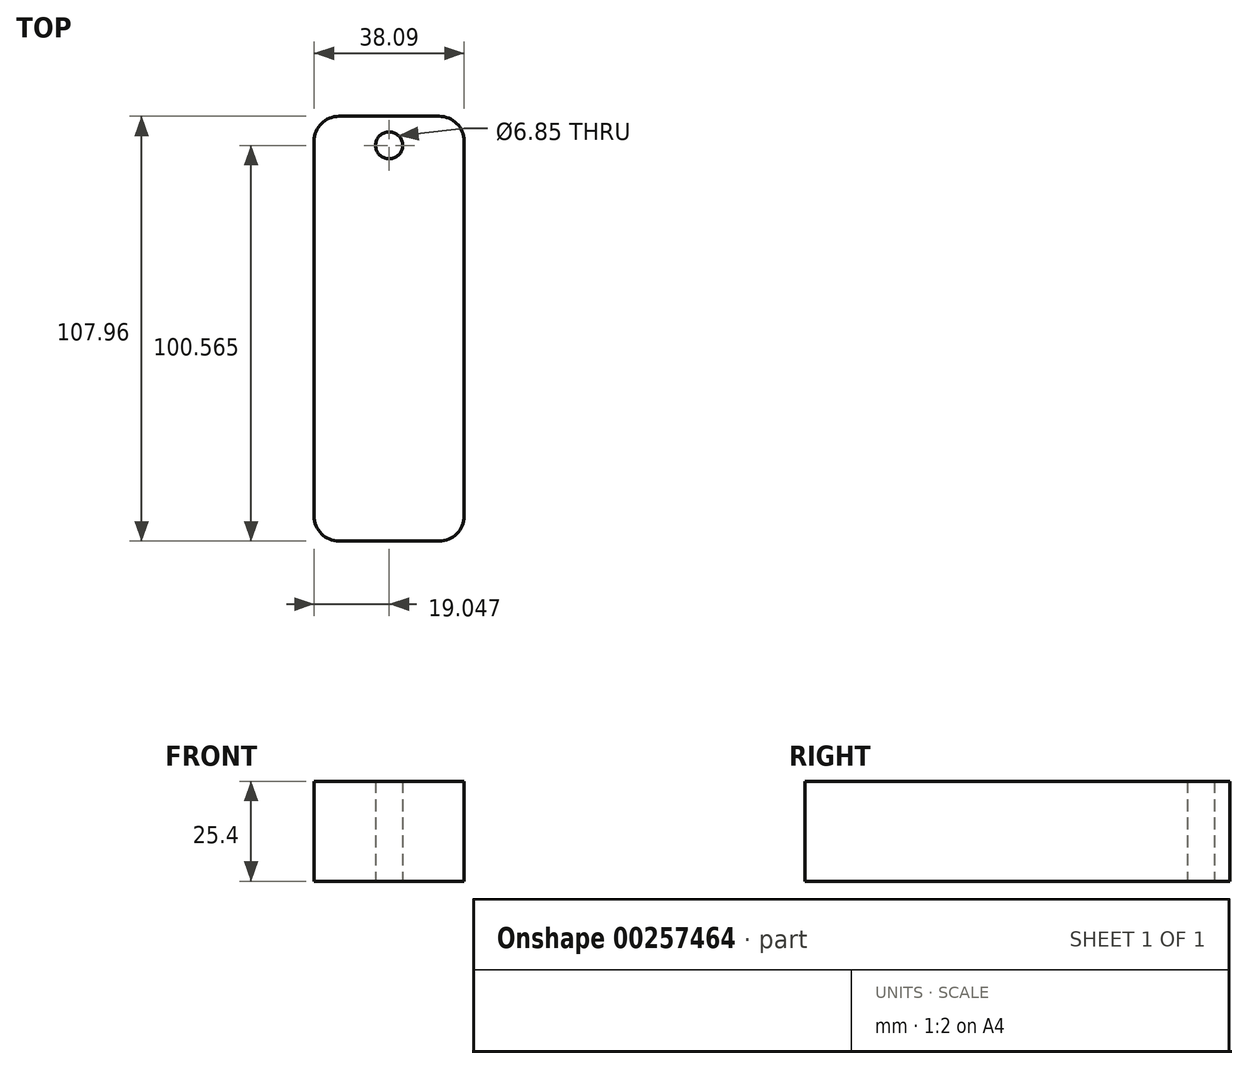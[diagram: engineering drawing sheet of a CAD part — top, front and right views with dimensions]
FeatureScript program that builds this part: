
annotation { "Feature Type Name" : "Feature", "Feature Type Description" : "" }
export const myFeature = defineFeature(function(context is Context, id is Id, definition is map)
    precondition{}
    {
        {
            var Q0;
            Q0=qCreatedBy(makeId("Top.planeOp"),FACE);
            var sketch = newSketch(context, id + "F0", { "sketchPlane" : qUnion([Q0])});
            skLineSegment(sketch, "E0.bottom", {"start": v(-19.4, 35.07) * mm, "end": v(5.98, 35.07) * mm});
            skLineSegment(sketch, "E0.top", {"start": v(-19.4, -72.89) * mm, "end": v(5.98, -72.89) * mm});
            skLineSegment(sketch, "E0.left", {"start": v(-25.76, 28.72) * mm, "end": v(-25.76, -66.54) * mm});
            skLineSegment(sketch, "E0.right", {"start": v(12.33, 28.72) * mm, "end": v(12.33, -66.54) * mm});
            skCircle(sketch, "E1", {"center": v(-6.71, 27.67) * mm, "radius": 3.43 * mm});
            skPoint(sketch, "E1.centerSnap0", {"position": v(-6.71, 35.07) * mm});
            skPoint(sketch, "E2.visualSharp", {"position": v(-25.76, 35.07) * mm});
            skArc(sketch, "E2.filletArc", {"start": v(-19.4, 35.07) * mm, "mid": v(-23.9, 33.21) * mm, "end": v(-25.76, 28.72) * mm});
            skPoint(sketch, "E3.visualSharp", {"position": v(12.33, 35.07) * mm});
            skArc(sketch, "E3.filletArc", {"start": v(12.33, 28.72) * mm, "mid": v(10.47, 33.21) * mm, "end": v(5.98, 35.07) * mm});
            skPoint(sketch, "E4.visualSharp", {"position": v(-25.76, -72.89) * mm});
            skArc(sketch, "E4.filletArc", {"start": v(-25.76, -66.54) * mm, "mid": v(-23.9, -71.03) * mm, "end": v(-19.4, -72.89) * mm});
            skPoint(sketch, "E5.visualSharp", {"position": v(12.33, -72.89) * mm});
            skArc(sketch, "E5.filletArc", {"start": v(5.98, -72.89) * mm, "mid": v(10.47, -71.03) * mm, "end": v(12.33, -66.54) * mm});
            skSolve(sketch);
        }
        {
            var Q0;
            Q0=makeQuery(id+"F0.imprint","IMPRINT",FACE,{"disambiguationData":[TD([[makeQuery(id+"F0.imprint","IMPRINT",EDGE,{"derivedFrom":sQuery(id+"F0.wireOp",EDGE,"E0.bottom")}),-1.0]])]});
            extrude(context, id + "F1", {"entities" : qUnion([Q0]), "depth" : 25.4 * mm});
        }
    });
